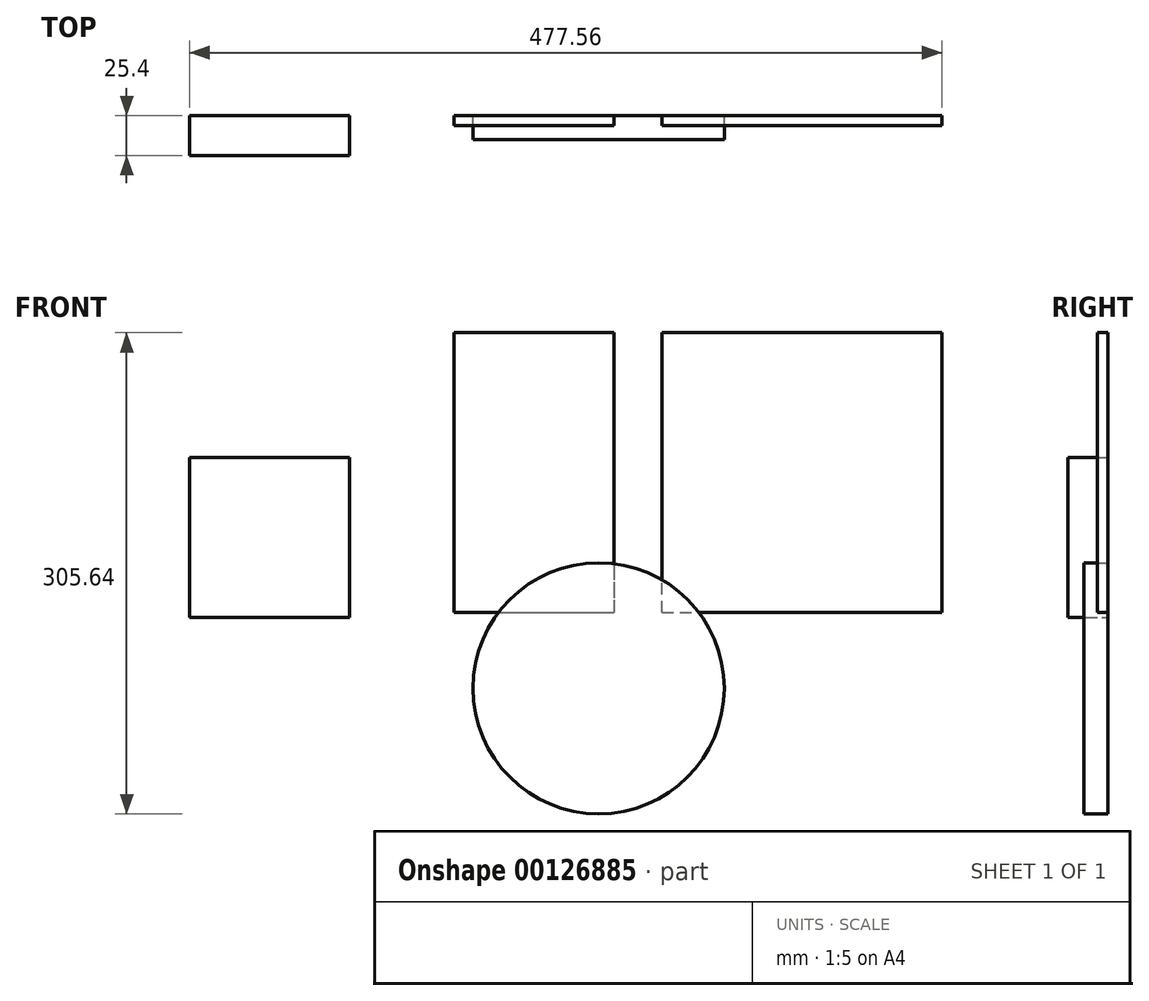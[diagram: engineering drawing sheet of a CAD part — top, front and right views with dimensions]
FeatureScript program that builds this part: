
annotation { "Feature Type Name" : "Feature", "Feature Type Description" : "" }
export const myFeature = defineFeature(function(context is Context, id is Id, definition is map)
    precondition{}
    {
        {
            var Q0;
            Q0=qCreatedBy(makeId("Front.planeOp"),FACE);
            var sketch = newSketch(context, id + "F0", { "sketchPlane" : qUnion([Q0])});
            skLineSegment(sketch, "E0.bottom", {"start": v(0, 0) * mm, "end": v(177.8, 0) * mm});
            skLineSegment(sketch, "E0.top", {"start": v(0, 177.8) * mm, "end": v(177.8, 177.8) * mm});
            skLineSegment(sketch, "E0.left", {"start": v(0, 0) * mm, "end": v(0, 177.8) * mm});
            skLineSegment(sketch, "E0.right", {"start": v(177.8, 0) * mm, "end": v(177.8, 177.8) * mm});
            skSolve(sketch);
        }
        {
            var Q0;
            Q0=qCreatedBy(makeId("Front.planeOp"),FACE);
            var sketch = newSketch(context, id + "F1", { "sketchPlane" : qUnion([Q0])});
            skLineSegment(sketch, "E1.bottom", {"start": v(-131.9, 177.8) * mm, "end": v(-30.3, 177.8) * mm});
            skLineSegment(sketch, "E1.top", {"start": v(-131.9, 0) * mm, "end": v(-30.3, 0) * mm});
            skLineSegment(sketch, "E1.left", {"start": v(-131.9, 177.8) * mm, "end": v(-131.9, 0) * mm});
            skLineSegment(sketch, "E1.right", {"start": v(-30.3, 177.8) * mm, "end": v(-30.3, 0) * mm});
            skSolve(sketch);
        }
        {
            var Q0;
            Q0=makeQuery(id+"F0.imprint","IMPRINT",FACE,{"disambiguationData":[TD([[makeQuery(id+"F0.imprint","IMPRINT",EDGE,{"derivedFrom":sQuery(id+"F0.wireOp",EDGE,"E0.bottom")}),1.0]])]});
            extrude(context, id + "F2", {"entities" : qUnion([Q0]), "depth" : 6.35 * mm});
        }
        {
            var Q0;
            Q0=makeQuery(id+"F1.imprint","IMPRINT",FACE,{"disambiguationData":[TD([[makeQuery(id+"F1.imprint","IMPRINT",EDGE,{"derivedFrom":sQuery(id+"F1.wireOp",EDGE,"E1.bottom")}),-1.0]])]});
            extrude(context, id + "F3", {"entities" : qUnion([Q0]), "depth" : 6.35 * mm});
        }
        {
            var Q0;
            Q0=qCreatedBy(makeId("Front.planeOp"),FACE);
            var sketch = newSketch(context, id + "F4", { "sketchPlane" : qUnion([Q0])});
            skCircle(sketch, "E2", {"center": v(-40.08, -48.08) * mm, "radius": 79.76 * mm});
            skSolve(sketch);
        }
        {
            var Q0;
            Q0=makeQuery(id+"F4.imprint","IMPRINT",FACE,{"disambiguationData":[TD([[makeQuery(id+"F4.imprint","IMPRINT",EDGE,{"derivedFrom":sQuery(id+"F4.wireOp",EDGE,"E2")}),1.0]])]});
            extrude(context, id + "F5", {"entities" : qUnion([Q0]), "depth" : 15.24 * mm});
        }
        {
            var Q0;
            Q0=qCreatedBy(makeId("Front.planeOp"),FACE);
            var sketch = newSketch(context, id + "F6", { "sketchPlane" : qUnion([Q0])});
            skLineSegment(sketch, "E3.bottom", {"start": v(-299.76, 98.57) * mm, "end": v(-198.16, 98.57) * mm});
            skLineSegment(sketch, "E3.top", {"start": v(-299.76, -3.03) * mm, "end": v(-198.16, -3.03) * mm});
            skLineSegment(sketch, "E3.left", {"start": v(-299.76, 98.57) * mm, "end": v(-299.76, -3.03) * mm});
            skLineSegment(sketch, "E3.right", {"start": v(-198.16, 98.57) * mm, "end": v(-198.16, -3.03) * mm});
            skSolve(sketch);
        }
        {
            var Q0;
            Q0=makeQuery(id+"F6.imprint","IMPRINT",FACE,{"disambiguationData":[TD([[makeQuery(id+"F6.imprint","IMPRINT",EDGE,{"derivedFrom":sQuery(id+"F6.wireOp",EDGE,"E3.bottom")}),-1.0]])]});
            extrude(context, id + "F7", {"entities" : qUnion([Q0]), "depth" : 25.4 * mm});
        }
    });
